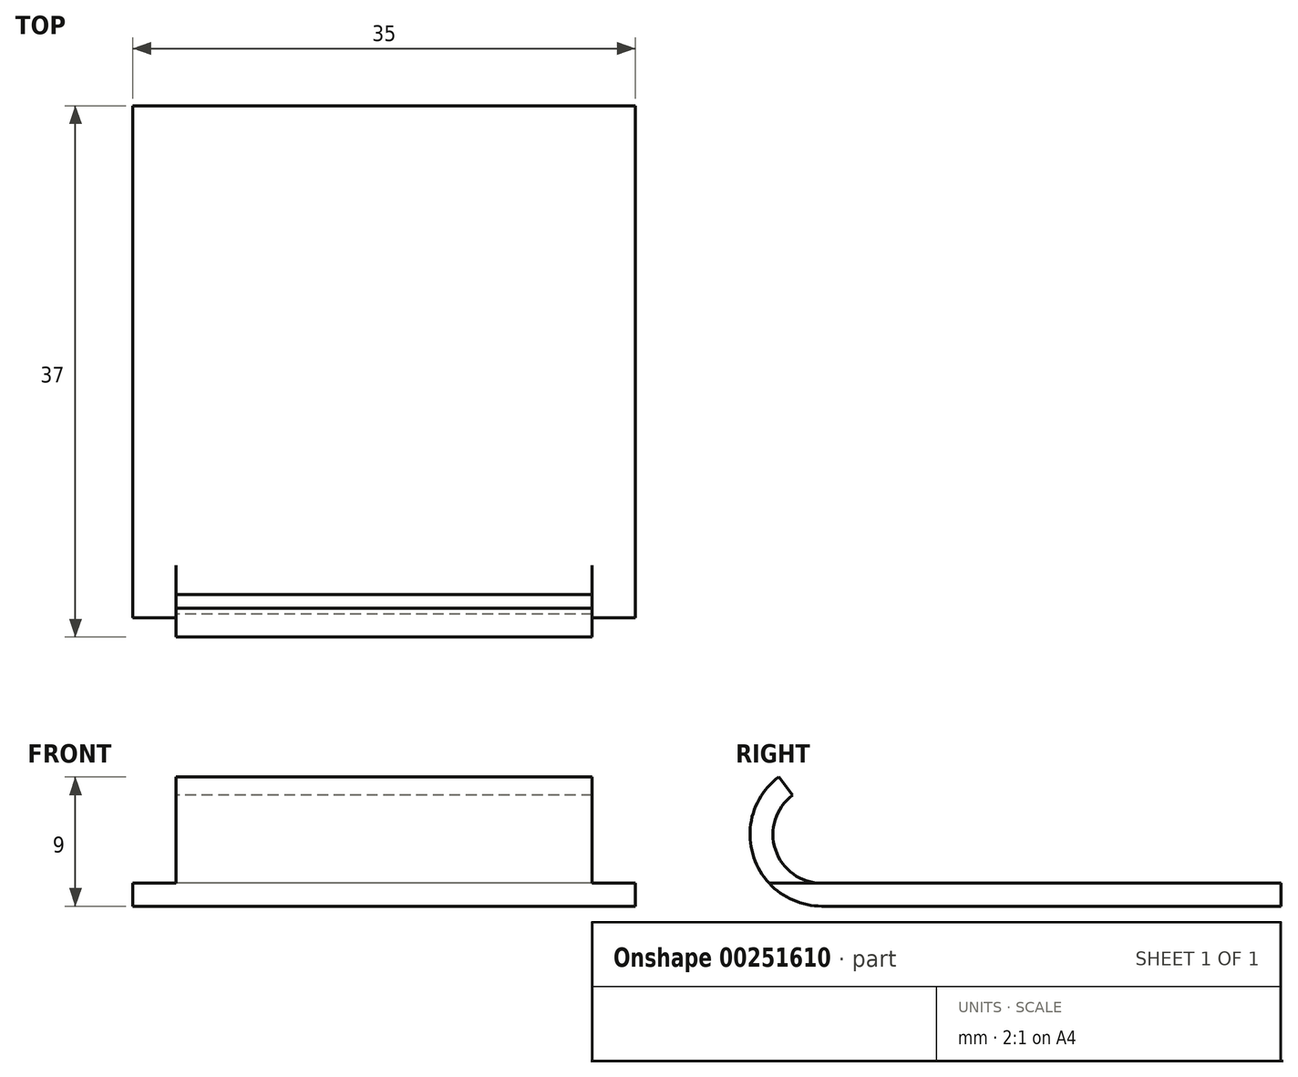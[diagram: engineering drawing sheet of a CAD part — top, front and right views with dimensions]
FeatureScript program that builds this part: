
annotation { "Feature Type Name" : "Feature", "Feature Type Description" : "" }
export const myFeature = defineFeature(function(context is Context, id is Id, definition is map)
    precondition{}
    {
        {
            var Q0;
            Q0=qCreatedBy(makeId("Right.planeOp"),FACE);
            var sketch = newSketch(context, id + "F0", { "sketchPlane" : qUnion([Q0])});
            skArc(sketch, "E0", {"start": v(-3, 9) * mm, "mid": v(-4.74, 3.42) * mm, "end": v(0, 0) * mm});
            skLineSegment(sketch, "E1", {"start": v(0, 0) * mm, "end": v(32, 0) * mm});
            skSolve(sketch);
        }
        {
            var Q0;
            Q0=qCreatedBy(makeId("Front.planeOp"),FACE);
            var sketch = newSketch(context, id + "F1", { "sketchPlane" : qUnion([Q0])});
            skLineSegment(sketch, "E2.bottom", {"start": v(35, 0) * mm, "end": v(0, 0) * mm});
            skLineSegment(sketch, "E2.top", {"start": v(35, 1.6) * mm, "end": v(0, 1.6) * mm});
            skLineSegment(sketch, "E2.left", {"start": v(35, 0) * mm, "end": v(35, 1.6) * mm});
            skLineSegment(sketch, "E2.right", {"start": v(0, 0) * mm, "end": v(0, 1.6) * mm});
            skSolve(sketch);
        }
        {
            var Q0;
            Q0=makeQuery(id+"F1.imprint","IMPRINT",FACE,{"disambiguationData":[TD([[makeQuery(id+"F1.imprint","IMPRINT",EDGE,{"derivedFrom":sQuery(id+"F1.wireOp",EDGE,"E2.bottom")}),-1.0]])]});
            var Q1;
            Q1=sQuery(id+"F0.wireOp",EDGE,"E0");
            sweep(context, id + "F2", {"profiles" : qUnion([Q0]), "path" : qUnion([Q1])});
        }
        {
            var Q0;
            Q0=makeQuery(id+"F1.imprint","IMPRINT",FACE,{"disambiguationData":[TD([[makeQuery(id+"F1.imprint","IMPRINT",EDGE,{"derivedFrom":sQuery(id+"F1.wireOp",EDGE,"E2.bottom")}),-1.0]])]});
            var Q1;
            Q1=sQuery(id+"F0.wireOp",EDGE,"E1");
            sweep(context, id + "F3", {"operationType" : NewBodyOperationType.ADD, "profiles" : qUnion([Q0]), "path" : qUnion([Q1])});
        }
        {
            var Q0;
            Q0=qCreatedBy(makeId("Front.planeOp"),FACE);
            var sketch = newSketch(context, id + "F4", { "sketchPlane" : qUnion([Q0])});
            skLineSegment(sketch, "E3.bottom", {"start": v(0, 9.6) * mm, "end": v(3, 9.6) * mm});
            skLineSegment(sketch, "E3.top", {"start": v(0, 1.6) * mm, "end": v(3, 1.6) * mm});
            skLineSegment(sketch, "E3.left", {"start": v(0, 9.6) * mm, "end": v(0, 1.6) * mm});
            skLineSegment(sketch, "E3.right", {"start": v(3, 9.6) * mm, "end": v(3, 1.6) * mm});
            skLineSegment(sketch, "E4.bottom", {"start": v(35, 1.6) * mm, "end": v(32, 1.6) * mm});
            skLineSegment(sketch, "E4.top", {"start": v(35, 9.6) * mm, "end": v(32, 9.6) * mm});
            skLineSegment(sketch, "E4.left", {"start": v(35, 1.6) * mm, "end": v(35, 9.6) * mm});
            skLineSegment(sketch, "E4.right", {"start": v(32, 1.6) * mm, "end": v(32, 9.6) * mm});
            skSolve(sketch);
        }
        {
            var Q0;
            Q0 = qSketchRegion(id + "F4", true);
            extrude(context, id + "F5", {"entities" : qUnion([Q0]), "operationType" : NewBodyOperationType.REMOVE, "endBound" : BoundingType.THROUGH_ALL, "depth" : 25 * mm});
        }
    });
